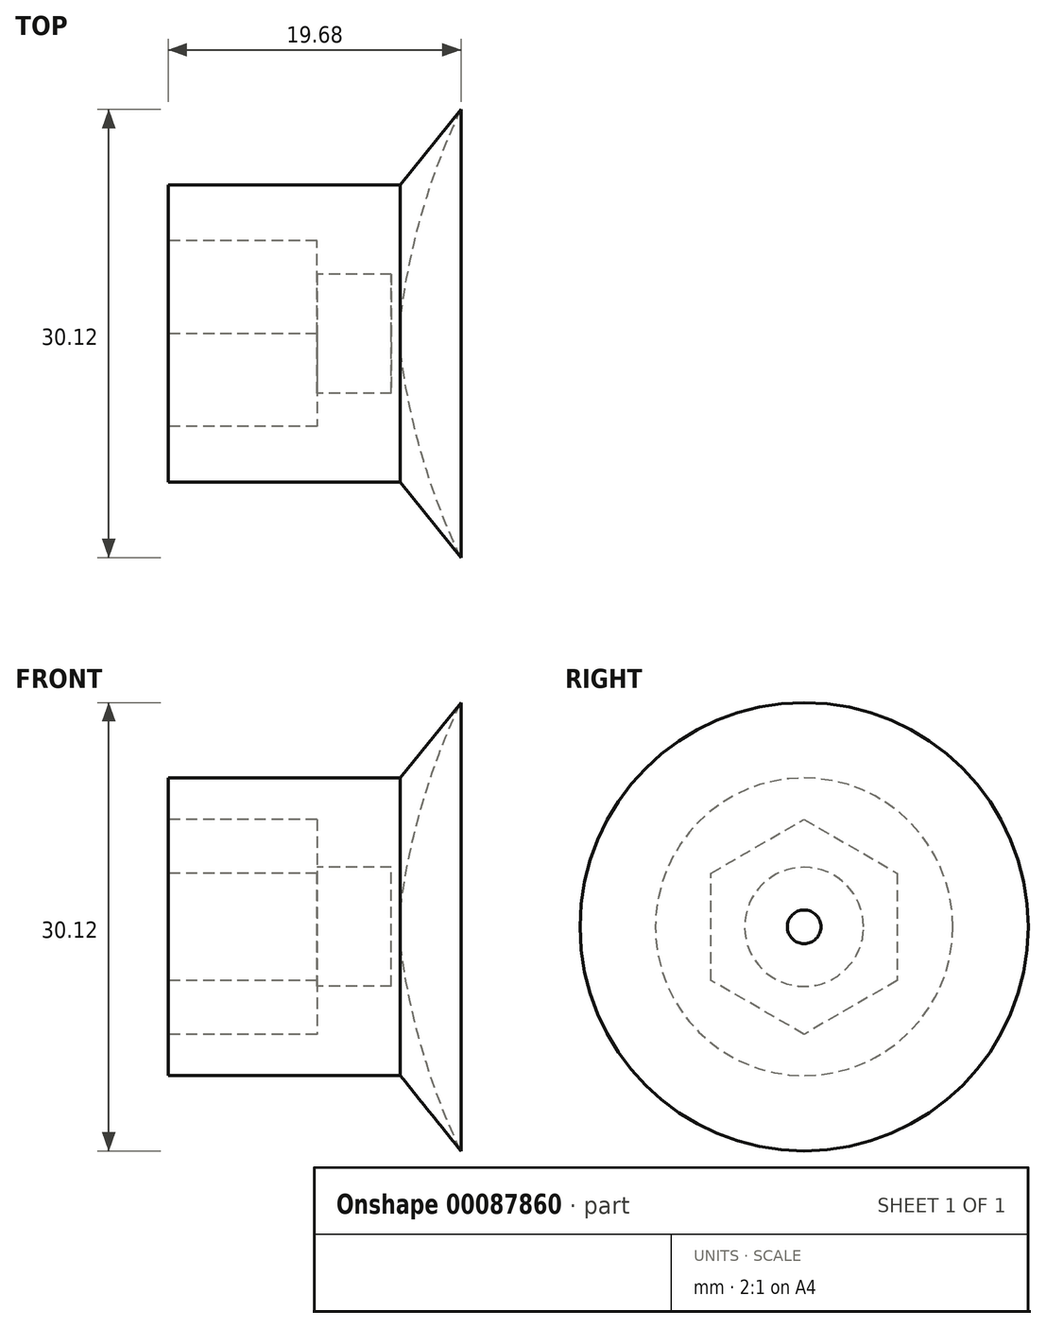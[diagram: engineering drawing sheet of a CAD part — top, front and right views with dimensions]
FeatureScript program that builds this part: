
annotation { "Feature Type Name" : "Feature", "Feature Type Description" : "" }
export const myFeature = defineFeature(function(context is Context, id is Id, definition is map)
    precondition{}
    {
        {
            var Q0;
            Q0=qCreatedBy(makeId("Right.planeOp"),FACE);
            var sketch = newSketch(context, id + "F0", { "sketchPlane" : qUnion([Q0])});
            skCircle(sketch, "E0", {"center": v(0, 0) * mm, "radius": 10 * mm});
            skCircle(sketch, "E1.cCircle", {"center": v(0, 0) * mm, "radius": 6.25 * mm, "construction": true});
            skLineSegment(sketch, "E1.0", {"start": v(6.25, 3.6) * mm, "end": v(6.25, -3.6) * mm});
            skLineSegment(sketch, "E1.1", {"start": v(6.25, -3.6) * mm, "end": v(0, -7.22) * mm});
            skLineSegment(sketch, "E1.2", {"start": v(0, -7.22) * mm, "end": v(-6.25, -3.6) * mm});
            skLineSegment(sketch, "E1.3", {"start": v(-6.25, -3.6) * mm, "end": v(-6.25, 3.6) * mm});
            skLineSegment(sketch, "E1.4", {"start": v(-6.25, 3.6) * mm, "end": v(0, 7.22) * mm});
            skLineSegment(sketch, "E1.5", {"start": v(0, 7.22) * mm, "end": v(6.25, 3.6) * mm});
            skPoint(sketch, "E1.0.midPoint", {"position": v(6.25, 0) * mm});
            skSolve(sketch);
        }
        {
            var Q0;
            Q0=makeQuery(id+"F0.imprint","IMPRINT",FACE,{"disambiguationData":[TD([[makeQuery(id+"F0.imprint","IMPRINT",EDGE,{"derivedFrom":sQuery(id+"F0.wireOp",EDGE,"E0")}),1.0]])]});
            extrude(context, id + "F1", {"entities" : qUnion([Q0]), "depth" : 10 * mm});
        }
        {
            var Q0;
            Q0=makeQuery(id+"F1.opExtrude","CAP_FACE",FACE,{"disambiguationData":[OSD([sQuery(id+"F0.wireOp",EDGE,"E0"),sQuery(id+"F0.wireOp",EDGE,"E1.0"),sQuery(id+"F0.wireOp",EDGE,"E1.1"),sQuery(id+"F0.wireOp",EDGE,"E1.2"),sQuery(id+"F0.wireOp",EDGE,"E1.3"),sQuery(id+"F0.wireOp",EDGE,"E1.4"),sQuery(id+"F0.wireOp",EDGE,"E1.5")])],"isStart":false});
            var sketch = newSketch(context, id + "F2", { "sketchPlane" : qUnion([Q0])});
            skCircle(sketch, "E2.0", {"center": v(0, 0) * mm, "radius": 10 * mm});
            skCircle(sketch, "E3", {"center": v(0, 0) * mm, "radius": 4 * mm});
            skSolve(sketch);
        }
        {
            var Q0;
            Q0=makeQuery(id+"F2.imprint","IMPRINT",FACE,{"disambiguationData":[TD([[makeQuery(id+"F2.imprint","IMPRINT",EDGE,{"derivedFrom":sQuery(id+"F2.wireOp",EDGE,"E3")}),-1.0]])]});
            var Q1;
            Q1=makeQuery(id+"F2.imprint","IMPRINT",FACE,{"disambiguationData":[TD([[makeQuery(id+"F2.imprint","IMPRINT",EDGE,{"derivedFrom":sQuery(id+"F2.wireOp",EDGE,"E2.0")}),1.0]])]});
            extrude(context, id + "F3", {"entities" : qUnion([Q0, Q1]), "operationType" : NewBodyOperationType.ADD, "depth" : 5 * mm});
        }
        {
            var Q0;
            Q0=makeQuery(id+"F3.opExtrude","CAP_FACE",FACE,{"disambiguationData":[OSD([sQuery(id+"F2.wireOp",EDGE,"E2.0"),sQuery(id+"F2.wireOp",EDGE,"E3")])],"isStart":false});
            var sketch = newSketch(context, id + "F4", { "sketchPlane" : qUnion([Q0])});
            skCircle(sketch, "E4.0", {"center": v(0, 0) * mm, "radius": 10 * mm});
            skSolve(sketch);
        }
        {
            var Q0;
            Q0 = qSketchRegion(id + "F4", true);
            extrude(context, id + "F5", {"entities" : qUnion([Q0]), "operationType" : NewBodyOperationType.ADD, "depth" : .6 * mm});
        }
        {
            var Q0;
            Q0=qCreatedBy(makeId("Front.planeOp"),FACE);
            var sketch = newSketch(context, id + "F6", { "sketchPlane" : qUnion([Q0])});
            skLineSegment(sketch, "E5.0", {"start": v(15.6, 10) * mm, "end": v(15.6, -10) * mm});
            skLineSegment(sketch, "E6", {"start": v(15.6, -10) * mm, "end": v(19.68, -15.06) * mm});
            skLineSegment(sketch, "E7", {"start": v(0, 0) * mm, "end": v(22.2, 0) * mm});
            skArc(sketch, "E8", {"start": v(15.6, 10) * mm, "mid": v(15.84, -2.82) * mm, "end": v(19.68, -15.06) * mm});
            skSolve(sketch);
        }
        {
            var Q0;
            {var subQ0=sQuery(id+"F6.wireOp",EDGE,"E6");Q0=makeQuery(id+"F6.imprint","IMPRINT",FACE,{"disambiguationData":[TD([[makeQuery(id+"F6.imprint","IMPRINT",EDGE,{"derivedFrom":subQ0}),1.0]])]});}
            var Q1;
            Q1=sQuery(id+"F6.wireOp",EDGE,"E7");
            revolve(context, id + "F7", {"operationType" : NewBodyOperationType.ADD, "entities" : qUnion([Q0]), "axis" : qUnion([Q1]), "revolveType" : RevolveType.FULL});
        }
    });
